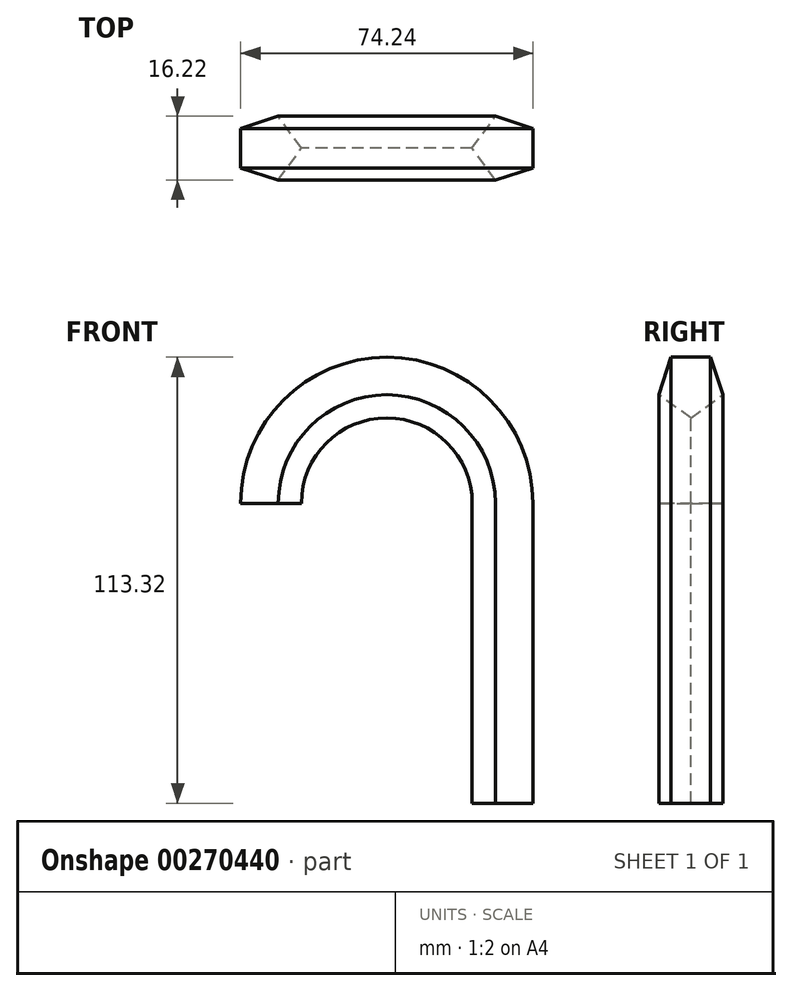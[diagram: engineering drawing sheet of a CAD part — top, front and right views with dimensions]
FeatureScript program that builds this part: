
annotation { "Feature Type Name" : "Feature", "Feature Type Description" : "" }
export const myFeature = defineFeature(function(context is Context, id is Id, definition is map)
    precondition{}
    {
        {
            var Q0;
            Q0=qCreatedBy(makeId("Front.planeOp"),FACE);
            var sketch = newSketch(context, id + "F0", { "sketchPlane" : qUnion([Q0])});
            skLineSegment(sketch, "E0", {"start": v(0, 0) * mm, "end": v(0, 76.2) * mm});
            skArc(sketch, "E1", {"start": v(0, 76.2) * mm, "mid": v(-30.22, 106.42) * mm, "end": v(-60.44, 76.2) * mm});
            skSolve(sketch);
        }
        {
            var Q0;
            Q0=qCreatedBy(makeId("Top.planeOp"),FACE);
            var sketch = newSketch(context, id + "F1", { "sketchPlane" : qUnion([Q0])});
            skCircle(sketch, "E2.cCircle", {"center": v(0, 0) * mm, "radius": 6.9 * mm, "construction": true});
            skLineSegment(sketch, "E2.0", {"start": v(6.9, 5.01) * mm, "end": v(6.9, -5.01) * mm});
            skLineSegment(sketch, "E2.1", {"start": v(6.9, -5.01) * mm, "end": v(-2.63, -8.1) * mm});
            skLineSegment(sketch, "E2.2", {"start": v(-2.63, -8.1) * mm, "end": v(-8.53, 0) * mm});
            skLineSegment(sketch, "E2.3", {"start": v(-8.53, 0) * mm, "end": v(-2.63, 8.1) * mm});
            skLineSegment(sketch, "E2.4", {"start": v(-2.63, 8.1) * mm, "end": v(6.9, 5.01) * mm});
            skPoint(sketch, "E2.0.midPoint", {"position": v(6.9, 0) * mm});
            skSolve(sketch);
        }
        {
            var Q0;
            Q0=makeQuery(id+"F1.imprint","IMPRINT",FACE,{"disambiguationData":[TD([[makeQuery(id+"F1.imprint","IMPRINT",EDGE,{"derivedFrom":sQuery(id+"F1.wireOp",EDGE,"E2.0")}),-1.0]])]});
            var Q1;
            Q1=sQuery(id+"F0.wireOp",EDGE,"E0");
            var Q2;
            Q2=sQuery(id+"F0.wireOp",EDGE,"E1");
            sweep(context, id + "F2", {"profiles" : qUnion([Q0]), "path" : qUnion([Q1, Q2])});
        }
    });
